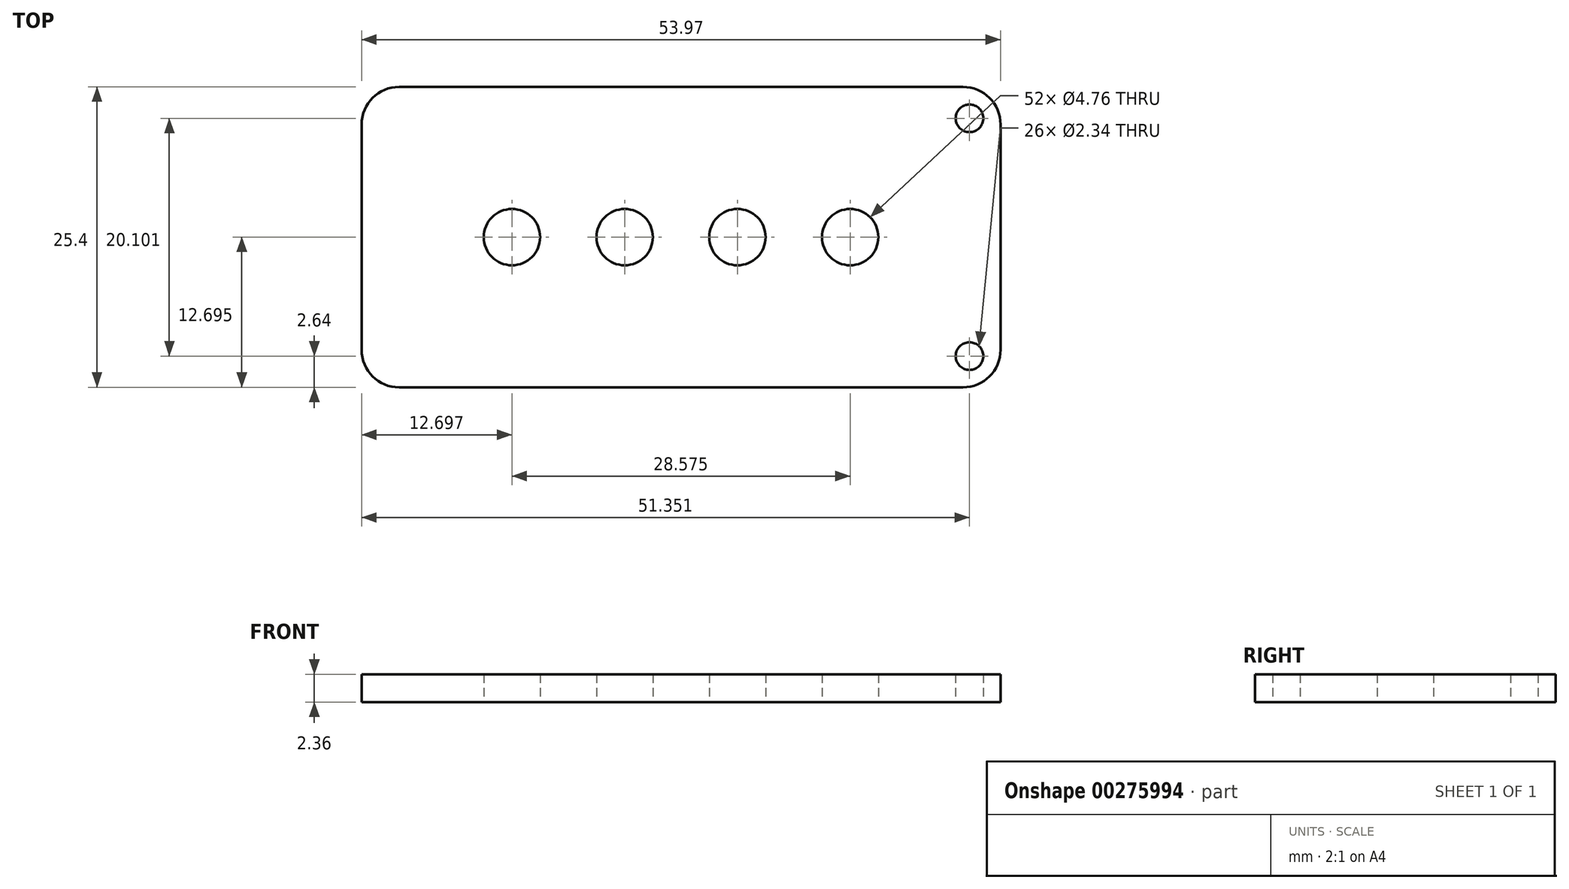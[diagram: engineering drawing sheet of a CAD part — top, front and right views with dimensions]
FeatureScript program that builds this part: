
annotation { "Feature Type Name" : "Feature", "Feature Type Description" : "" }
export const myFeature = defineFeature(function(context is Context, id is Id, definition is map)
    precondition{}
    {
        {
            var Q0;
            Q0=qCreatedBy(makeId("Top.planeOp"),FACE);
            var sketch = newSketch(context, id + "F0", { "sketchPlane" : qUnion([Q0])});
            skLineSegment(sketch, "E0.bottom", {"start": v(23.83, 12.7) * mm, "end": v(-23.8, 12.7) * mm});
            skLineSegment(sketch, "E0.top", {"start": v(23.83, -12.7) * mm, "end": v(-23.8, -12.7) * mm});
            skLineSegment(sketch, "E0.left", {"start": v(27, 9.53) * mm, "end": v(27, -9.52) * mm});
            skLineSegment(sketch, "E0.right", {"start": v(-26.97, 9.53) * mm, "end": v(-26.97, -9.52) * mm});
            skPoint(sketch, "E0.middle", {"position": v(0, 0) * mm});
            skCircle(sketch, "E1", {"center": v(4.78, 0) * mm, "radius": 2.38 * mm});
            skCircle(sketch, "E2", {"center": v(14.3, 0) * mm, "radius": 2.38 * mm});
            skCircle(sketch, "E3.MirrorC", {"center": v(-4.75, 0) * mm, "radius": 2.38 * mm});
            skCircle(sketch, "E4.MirrorC", {"center": v(-14.27, 0) * mm, "radius": 2.38 * mm});
            skPoint(sketch, "E5.visualSharp", {"position": v(-26.97, 12.7) * mm});
            skArc(sketch, "E5.filletArc", {"start": v(-23.8, 12.7) * mm, "mid": v(-26.04, 11.78) * mm, "end": v(-26.97, 9.53) * mm});
            skPoint(sketch, "E6.visualSharp", {"position": v(27, 12.7) * mm});
            skArc(sketch, "E6.filletArc", {"start": v(27, 9.53) * mm, "mid": v(26.07, 11.78) * mm, "end": v(23.83, 12.7) * mm});
            skPoint(sketch, "E7.visualSharp", {"position": v(27, -12.7) * mm});
            skArc(sketch, "E7.filletArc", {"start": v(23.83, -12.7) * mm, "mid": v(26.07, -11.76) * mm, "end": v(27, -9.52) * mm});
            skPoint(sketch, "E8.visualSharp", {"position": v(-26.97, -12.7) * mm});
            skArc(sketch, "E8.filletArc", {"start": v(-26.97, -9.52) * mm, "mid": v(-26.04, -11.76) * mm, "end": v(-23.8, -12.7) * mm});
            skCircle(sketch, "E9", {"center": v(24.38, 10.05) * mm, "radius": 1.17 * mm});
            skCircle(sketch, "E10.MirrorC", {"center": v(24.38, -10.05) * mm, "radius": 1.17 * mm});
            skSolve(sketch);
        }
        {
            var Q0;
            Q0 = qSketchRegion(id + "F0", true);
            extrude(context, id + "F1", {"entities" : qUnion([Q0]), "depth" : 2.36 * mm});
        }
    });
